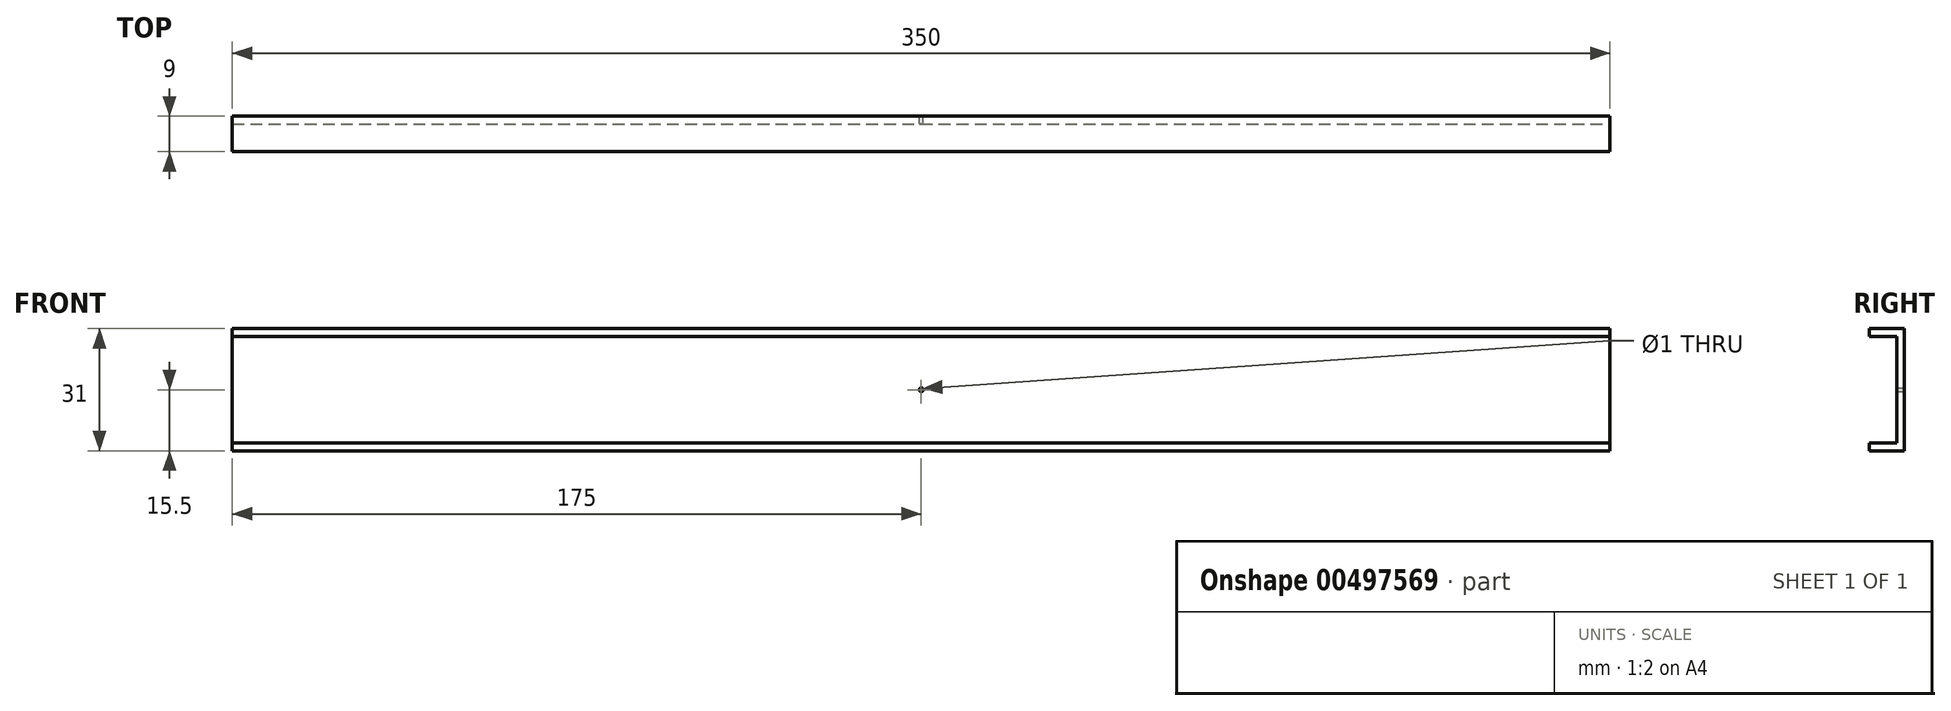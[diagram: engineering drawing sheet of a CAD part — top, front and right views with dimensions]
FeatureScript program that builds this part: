
annotation { "Feature Type Name" : "Feature", "Feature Type Description" : "" }
export const myFeature = defineFeature(function(context is Context, id is Id, definition is map)
    precondition{}
    {
        {
            var Q0;
            Q0=qCreatedBy(makeId("Front.planeOp"),FACE);
            var sketch = newSketch(context, id + "F0", { "sketchPlane" : qUnion([Q0])});
            skLineSegment(sketch, "E0.bottom", {"start": v(-175, 13.5) * mm, "end": v(175, 13.5) * mm});
            skLineSegment(sketch, "E0.top", {"start": v(-175, -17.5) * mm, "end": v(175, -17.5) * mm});
            skLineSegment(sketch, "E0.left", {"start": v(-175, 13.5) * mm, "end": v(-175, -17.5) * mm});
            skLineSegment(sketch, "E0.right", {"start": v(175, 13.5) * mm, "end": v(175, -17.5) * mm});
            skLineSegment(sketch, "E1.left", {"start": v(-175, 13.5) * mm, "end": v(-175, 11.5) * mm});
            skLineSegment(sketch, "E1.right", {"start": v(175, 13.5) * mm, "end": v(175, 11.5) * mm});
            skLineSegment(sketch, "E2.left", {"start": v(-175, -15.5) * mm, "end": v(-175, -17.5) * mm});
            skLineSegment(sketch, "E2.right", {"start": v(175, -15.5) * mm, "end": v(175, -17.5) * mm});
            skCircle(sketch, "E3", {"center": v(0, -2) * mm, "radius": 0.5 * mm});
            skSolve(sketch);
        }
        {
            var Q0;
            Q0 = qSketchRegion(id + "F0", true);
            extrude(context, id + "F1", {"entities" : qUnion([Q0]), "depth" : 2 * mm});
        }
        {
            var Q0;
            Q0=makeQuery(id+"F1.opExtrude","CAP_FACE",FACE,{"disambiguationData":[OSD([sQuery(id+"F0.wireOp",EDGE,"E0.left"),sQuery(id+"F0.wireOp",EDGE,"E0.right"),sQuery(id+"F0.wireOp",EDGE,"E0.bottom"),sQuery(id+"F0.wireOp",EDGE,"E1.left"),sQuery(id+"F0.wireOp",EDGE,"E1.right"),sQuery(id+"F0.wireOp",EDGE,"E0.top"),sQuery(id+"F0.wireOp",EDGE,"E2.left"),sQuery(id+"F0.wireOp",EDGE,"E2.right")])],"isStart":false});
            var sketch = newSketch(context, id + "F2", { "sketchPlane" : qUnion([Q0])});
            skLineSegment(sketch, "E4.bottom", {"start": v(-175, 13.5) * mm, "end": v(175, 13.5) * mm});
            skLineSegment(sketch, "E4.top", {"start": v(-175, 11.5) * mm, "end": v(175, 11.5) * mm});
            skLineSegment(sketch, "E4.left", {"start": v(-175, 13.5) * mm, "end": v(-175, 11.5) * mm});
            skLineSegment(sketch, "E4.right", {"start": v(175, 13.5) * mm, "end": v(175, 11.5) * mm});
            skLineSegment(sketch, "E5.bottom", {"start": v(-175, -17.5) * mm, "end": v(175, -17.5) * mm});
            skLineSegment(sketch, "E5.top", {"start": v(-175, -15.5) * mm, "end": v(175, -15.5) * mm});
            skLineSegment(sketch, "E5.left", {"start": v(-175, -17.5) * mm, "end": v(-175, -15.5) * mm});
            skLineSegment(sketch, "E5.right", {"start": v(175, -17.5) * mm, "end": v(175, -15.5) * mm});
            skSolve(sketch);
        }
        {
            var Q0;
            Q0=makeQuery(id+"F2.imprint","IMPRINT",FACE,{"disambiguationData":[TD([[makeQuery(id+"F2.imprint","IMPRINT",EDGE,{"derivedFrom":sQuery(id+"F2.wireOp",EDGE,"E4.bottom")}),-1.0]])]});
            var Q1;
            Q1=makeQuery(id+"F2.imprint","IMPRINT",FACE,{"disambiguationData":[TD([[makeQuery(id+"F2.imprint","IMPRINT",EDGE,{"derivedFrom":sQuery(id+"F2.wireOp",EDGE,"E5.bottom")}),1.0]])]});
            extrude(context, id + "F3", {"entities" : qUnion([Q0, Q1]), "operationType" : NewBodyOperationType.ADD, "depth" : 7 * mm});
        }
        {
            var Q0;
            Q0=makeQuery(id+"F1.opExtrude","SWEPT_BODY",BODY,{"disambiguationData":[OSD([sQuery(id+"F0.wireOp",EDGE,"E0.left"),sQuery(id+"F0.wireOp",EDGE,"E0.right"),sQuery(id+"F0.wireOp",EDGE,"E0.bottom"),sQuery(id+"F0.wireOp",EDGE,"E1.left"),sQuery(id+"F0.wireOp",EDGE,"E1.right"),sQuery(id+"F0.wireOp",EDGE,"E0.top"),sQuery(id+"F0.wireOp",EDGE,"E2.left"),sQuery(id+"F0.wireOp",EDGE,"E2.right")])]});
            transform(context, id + "F4", {"entities" : qUnion([Q0]), "transformType" : TransformType.TRANSLATION_3D, "dx" : 0 * mm, "dy" : 0 * mm, "dz" : 0 * mm, "makeCopy" : true});
        }
        {
            var Q0;
            Q0=makeQuery(id+"F4.opPattern","COPY",BODY,{"derivedFrom":makeQuery(id+"F1.opExtrude","SWEPT_BODY",BODY,{"disambiguationData":[OSD([sQuery(id+"F0.wireOp",EDGE,"E0.left"),sQuery(id+"F0.wireOp",EDGE,"E0.right"),sQuery(id+"F0.wireOp",EDGE,"E0.bottom"),sQuery(id+"F0.wireOp",EDGE,"E1.left"),sQuery(id+"F0.wireOp",EDGE,"E1.right"),sQuery(id+"F0.wireOp",EDGE,"E0.top"),sQuery(id+"F0.wireOp",EDGE,"E2.left"),sQuery(id+"F0.wireOp",EDGE,"E2.right")])]}),"instanceName":"1"});
            deleteBodies(context, id + "F5", {"entities" : qUnion([Q0])});
        }
        {
            var Q0;
            Q0 = qSketchRegion(id + "F0", true);
            extrude(context, id + "F6", {"entities" : qUnion([Q0]), "operationType" : NewBodyOperationType.REMOVE, "oppositeDirection" : true, "depth" : 2 * mm});
        }
    });
